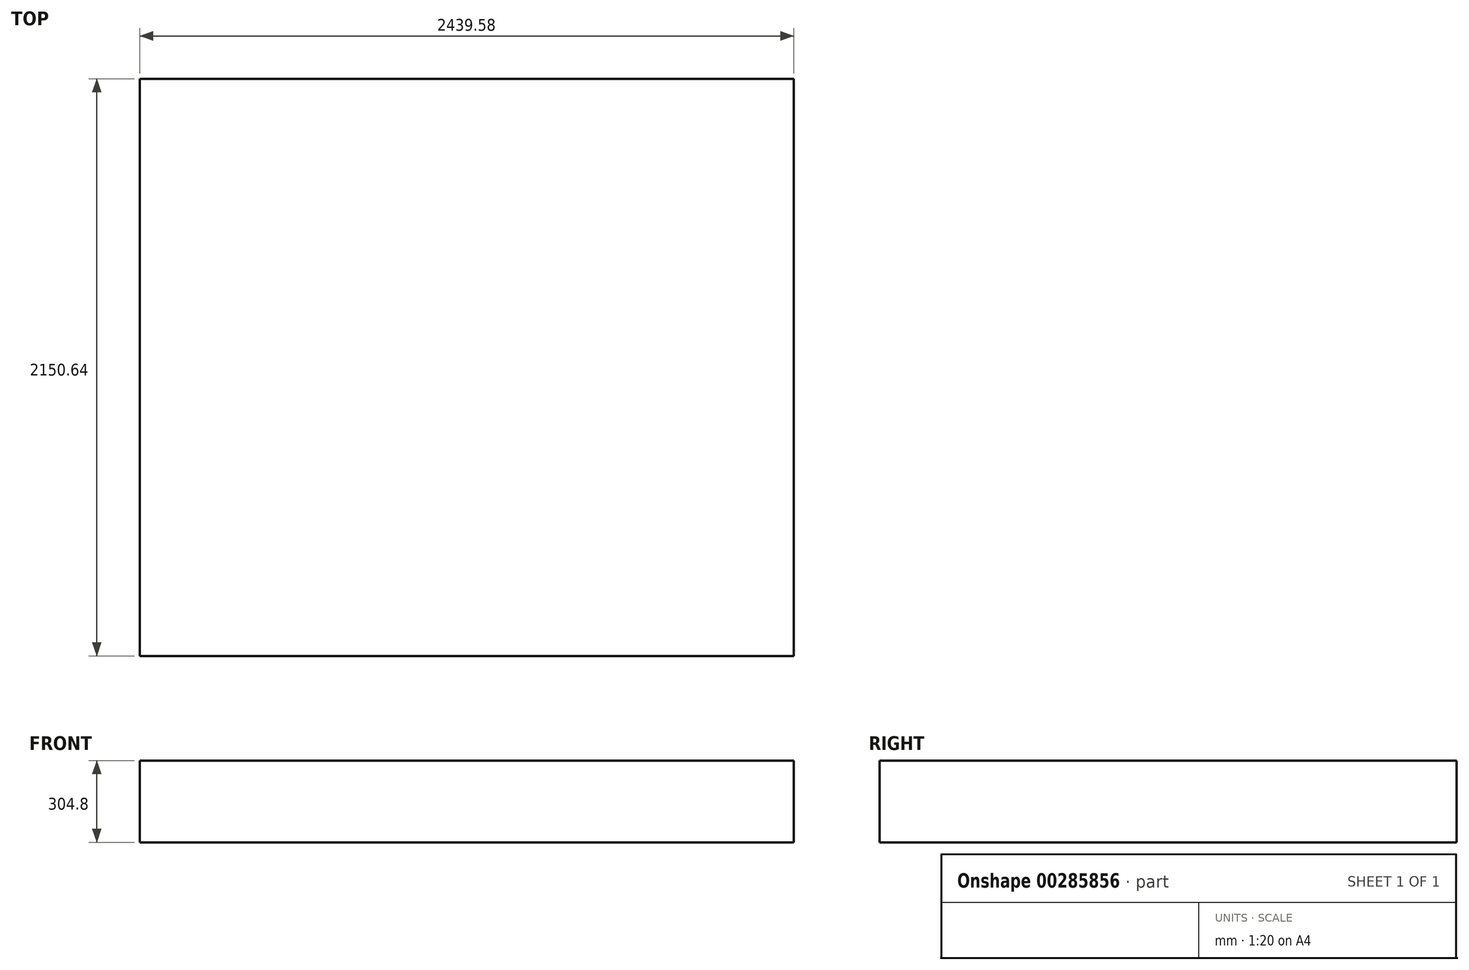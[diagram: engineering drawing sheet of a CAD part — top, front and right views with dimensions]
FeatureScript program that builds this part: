
annotation { "Feature Type Name" : "Feature", "Feature Type Description" : "" }
export const myFeature = defineFeature(function(context is Context, id is Id, definition is map)
    precondition{}
    {
        {
            var Q0;
            Q0=qCreatedBy(makeId("Top.planeOp"),FACE);
            var sketch = newSketch(context, id + "F0", { "sketchPlane" : qUnion([Q0])});
            skLineSegment(sketch, "E0.bottom", {"start": v(1219.79, -1075.32) * mm, "end": v(-1219.79, -1075.32) * mm});
            skLineSegment(sketch, "E0.top", {"start": v(1219.79, 1075.32) * mm, "end": v(-1219.79, 1075.32) * mm});
            skLineSegment(sketch, "E0.left", {"start": v(1219.79, -1075.32) * mm, "end": v(1219.79, 1075.32) * mm});
            skLineSegment(sketch, "E0.right", {"start": v(-1219.79, -1075.32) * mm, "end": v(-1219.79, 1075.32) * mm});
            skPoint(sketch, "E0.middle", {"position": v(0, 0) * mm});
            skSolve(sketch);
        }
        {
            var Q0;
            Q0=makeQuery(id+"F0.imprint","IMPRINT",FACE,{"disambiguationData":[TD([[makeQuery(id+"F0.imprint","IMPRINT",EDGE,{"derivedFrom":sQuery(id+"F0.wireOp",EDGE,"E0.bottom")}),-1.0]])]});
            extrude(context, id + "F1", {"entities" : qUnion([Q0]), "oppositeDirection" : true, "depth" : 304.8 * mm});
        }
    });
